# Revit family: HansWeitzel_2038
name_source: partatom
category: Allgemeines Modell
revit_build: Autodesk Revit 2017 (Build: 20160225_1515(x64)
units: mm (PartAtom-declared; Revit-internal decimal feet)

## family parameters
Basisbauteil = Wand
Beim Laden mit Abzugskörper schneiden = Nein
Bemaßung runder Anschluss = Durchmesser verwenden
Gemeinsam genutzt = Nein
Immer vertikal = Ja
Kann Basisbauteil für Bewehrung sein = Nein
Raumberechnungspunkt = Nein
Teiletyp = Normal

## types (1)
- Type 1
    BIM = https://media.live.bim.site
    BIMSITE_PRODUCT_ID = 413a913b2037ab60e957ac03be6171f74f8c57b7
    Beschreibung = HZ-Stoßverbinder SLF Buche dunkel für HZ-Sockelleiste SLF nur mit SCH2158
    Breite [mm] = 45
    Dekor = Buche dunkel
    Farbton = Holzart/Holzdekor
    GTIN = 4022023220018
    Gewicht unverpackt (netto) [kg] = 0.008
    HAN = 2038
    HeinzeBIM = https://www.heinze.de
    Hersteller = Hans Weitzel GmbH & Co. KG
    Höhe [mm] = 97
    Ist System = Nein
    Ist Zubehör = Nein
    Length1 = 50 mm  [stored 0.164042 ft]
    Length2 = 50 mm  [stored 0.164042 ft]
    Length3 = 50 mm  [stored 0.164042 ft]
    Menge pro Verpackungseinheit = 10
    Profilart = Anschlussprofi
    Tiefe (mm) = 30
    Typname = HZ-Stoßverbinder SLF Buche dunkel
    Wandmontage möglich = Ja
    Werkstoff = Acryl
    max. Betriebstemperatur (°C) = 90

note: [stored X ft] marks values corroborated as IEEE doubles in the binary element streams (Revit-internal decimal feet)

## geometry (parser evidence)
native form markers: Sweep x9
no freeform markers — native parametric forms only
